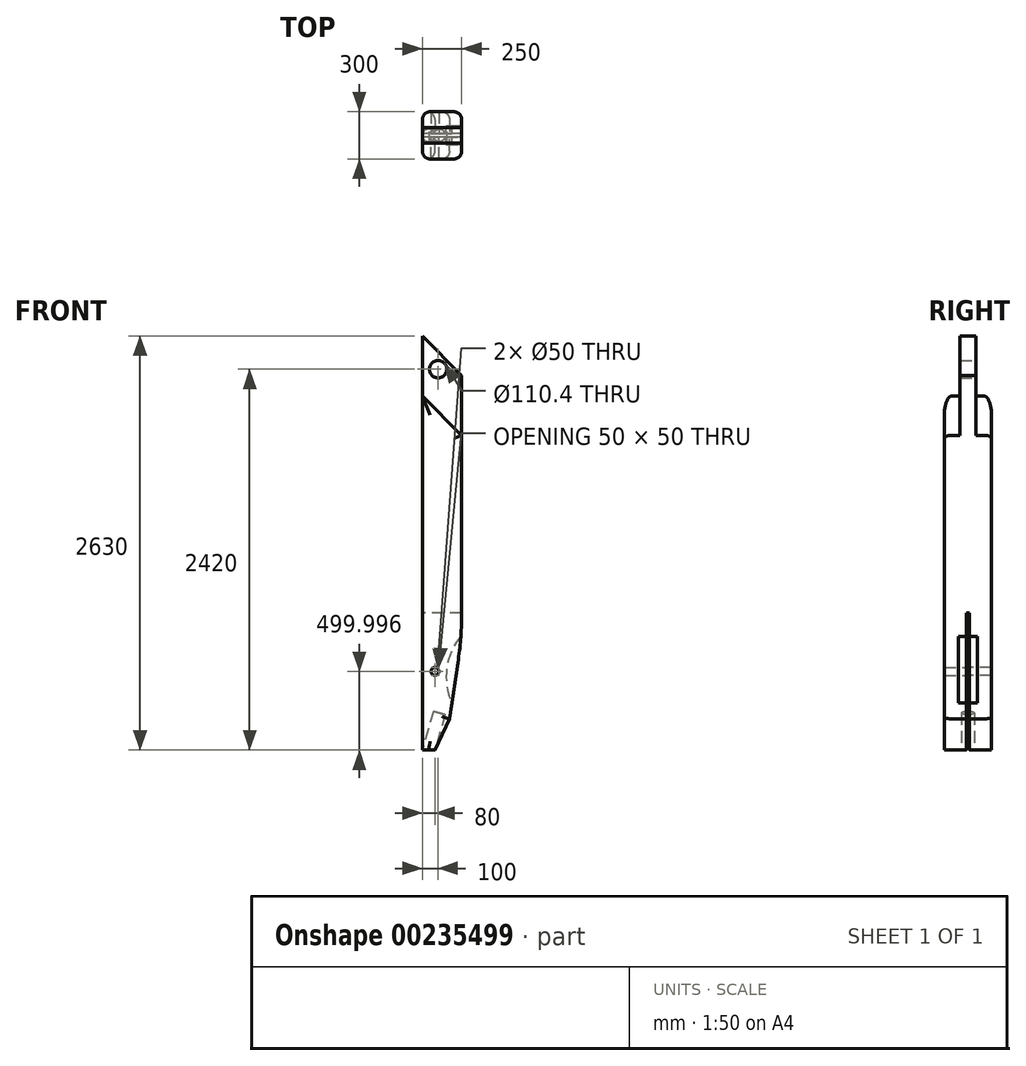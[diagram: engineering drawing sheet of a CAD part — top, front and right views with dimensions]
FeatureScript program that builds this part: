
annotation { "Feature Type Name" : "Feature", "Feature Type Description" : "" }
export const myFeature = defineFeature(function(context is Context, id is Id, definition is map)
    precondition{}
    {
        {
            var Q0;
            Q0=qCreatedBy(makeId("Front.planeOp"),FACE);
            var sketch = newSketch(context, id + "F0", { "sketchPlane" : qUnion([Q0])});
            skLineSegment(sketch, "E0", {"start": v(0, 1074.27) * mm, "end": v(0, -1175.73) * mm});
            skLineSegment(sketch, "E1", {"start": v(0, 1074.27) * mm, "end": v(0, 1454.27) * mm});
            skLineSegment(sketch, "E2", {"start": v(0, -1175.73) * mm, "end": v(80, -1175.73) * mm});
            skLineSegment(sketch, "E3", {"start": v(80, -1175.73) * mm, "end": v(172.42, -977.53) * mm});
            skLineSegment(sketch, "E4", {"start": v(250, -305.73) * mm, "end": v(250, 1204.27) * mm});
            skLineSegment(sketch, "E5", {"start": v(250, 1204.27) * mm, "end": v(0, 1454.27) * mm});
            skLineSegment(sketch, "E6", {"start": v(0, 1074.27) * mm, "end": v(250, 824.27) * mm});
            skCircle(sketch, "E7", {"center": v(80, -675.73) * mm, "radius": 25 * mm});
            skCircle(sketch, "E8", {"center": v(100, 1244.27) * mm, "radius": 55.2 * mm});
            skLineSegment(sketch, "E9", {"start": v(80, -532.98) * mm, "end": v(80, -1372.18) * mm, "construction": true});
            skLineSegment(sketch, "E10", {"start": v(0, 74.27) * mm, "end": v(250, 74.27) * mm, "construction": true});
            skLineSegment(sketch, "E11", {"start": v(172.42, -977.53) * mm, "end": v(228.5, -598.22) * mm});
            skArc(sketch, "E12", {"start": v(250, -305.73) * mm, "mid": v(244.62, -452.37) * mm, "end": v(228.5, -598.22) * mm});
            skSolve(sketch);
        }
        {
            var Q0;
            Q0=makeQuery(id+"F0.imprint","IMPRINT",FACE,{"disambiguationData":[TD([[makeQuery(id+"F0.imprint","IMPRINT",EDGE,{"derivedFrom":sQuery(id+"F0.wireOp",EDGE,"E0")}),1.0]])]});
            extrude(context, id + "F1", {"entities" : qUnion([Q0]), "depth" : 150 * mm});
        }
        {
            var Q0;
            Q0=makeQuery(id+"F0.imprint","IMPRINT",FACE,{"disambiguationData":[TD([[makeQuery(id+"F0.imprint","IMPRINT",EDGE,{"derivedFrom":sQuery(id+"F0.wireOp",EDGE,"E1")}),-1.0]])]});
            extrude(context, id + "F2", {"entities" : qUnion([Q0]), "operationType" : NewBodyOperationType.ADD, "depth" : 50 * mm});
        }
        {
            var Q0;
            Q0=makeQuery(id+"F2.boolean.opBoolean","MERGE",FACE,{"derivedFrom":[makeQuery(id+"F1.opExtrude","SWEPT_FACE",FACE,{"disambiguationData":[OSD([sQuery(id+"F0.wireOp",EDGE,"E0")])]}),makeQuery(id+"F2.opExtrude","SWEPT_FACE",FACE,{"disambiguationData":[OSD([sQuery(id+"F0.wireOp",EDGE,"E1")])]})]});
            var sketch = newSketch(context, id + "F3", { "sketchPlane" : qUnion([Q0])});
            skLineSegment(sketch, "E13.0", {"start": v(10, -305.73) * mm, "end": v(0, -305.73) * mm});
            skLineSegment(sketch, "E14", {"start": v(10, -305.73) * mm, "end": v(10, -1175.73) * mm});
            skPoint(sketch, "E15.orphan", {"position": v(150, -305.73) * mm});
            skLineSegment(sketch, "E16.0", {"start": v(0, -977.53) * mm, "end": v(0, -598.22) * mm});
            skLineSegment(sketch, "E17.0", {"start": v(0, -1175.73) * mm, "end": v(0, -977.53) * mm});
            skLineSegment(sketch, "E18.0", {"start": v(10, -1175.73) * mm, "end": v(0, -1175.73) * mm});
            skPoint(sketch, "E19.orphan", {"position": v(150, -1175.73) * mm});
            skLineSegment(sketch, "E20.0", {"start": v(0, -305.73) * mm, "end": v(0, -598.22) * mm});
            skSolve(sketch);
        }
        {
            var Q0;
            Q0 = qSketchRegion(id + "F3", true);
            extrude(context, id + "F4", {"entities" : qUnion([Q0]), "operationType" : NewBodyOperationType.REMOVE, "endBound" : BoundingType.THROUGH_ALL, "oppositeDirection" : true, "depth" : 25 * mm});
        }
        {
            var Q0;
            Q0=makeQuery(id+"F1.opExtrude","SWEPT_BODY",BODY,{"disambiguationData":[OSD([sQuery(id+"F0.wireOp",EDGE,"E0"),sQuery(id+"F0.wireOp",EDGE,"E2"),sQuery(id+"F0.wireOp",EDGE,"E3"),sQuery(id+"F0.wireOp",EDGE,"E4"),sQuery(id+"F0.wireOp",EDGE,"E6"),sQuery(id+"F0.wireOp",EDGE,"E7"),sQuery(id+"F0.wireOp",EDGE,"E11"),sQuery(id+"F0.wireOp",EDGE,"E12")])]});
            var Q1;
            Q1=qCreatedBy(makeId("Front.planeOp"),FACE);
            mirror(context, id + "F5", {"operationType" : NewBodyOperationType.ADD, "entities" : qUnion([Q0]), "mirrorPlane" : qUnion([Q1])});
        }
        {
            var Q0;
            Q0=makeQuery(id+"F5.opPattern","COPY",FACE,{"derivedFrom":makeQuery(id+"F1.opExtrude","CAP_FACE",FACE,{"disambiguationData":[OSD([sQuery(id+"F0.wireOp",EDGE,"E0"),sQuery(id+"F0.wireOp",EDGE,"E2"),sQuery(id+"F0.wireOp",EDGE,"E3"),sQuery(id+"F0.wireOp",EDGE,"E4"),sQuery(id+"F0.wireOp",EDGE,"E6"),sQuery(id+"F0.wireOp",EDGE,"E7"),sQuery(id+"F0.wireOp",EDGE,"E11"),sQuery(id+"F0.wireOp",EDGE,"E12")])],"isStart":false}),"instanceName":"1"});
            cPlane(context, id + "F6", {"entities" : qUnion([Q0]), "cplaneType" : CPlaneType.OFFSET, "offset" : 150 * mm, "oppositeDirection" : true, "width" : 150 * mm, "height" : 150 * mm});
        }
        {
            var Q0;
            Q0=qCreatedBy(id+"F6.planeOp",FACE);
            var sketch = newSketch(context, id + "F7", { "sketchPlane" : qUnion([Q0])});
            skLineSegment(sketch, "E21.0", {"start": v(-187.47, -875.73) * mm, "end": v(-228.5, -598.22) * mm});
            skPoint(sketch, "E22.0", {"position": v(-40, -1175.73) * mm});
            skPoint(sketch, "E23.0", {"position": v(-80, -1175.73) * mm});
            skPoint(sketch, "E24", {"position": v(-187.47, -875.73) * mm});
            skPoint(sketch, "E25.0", {"position": v(0, -1175.73) * mm});
            skPoint(sketch, "E26.0.start.orphan", {"position": v(-250, -305.73) * mm});
            skPoint(sketch, "E27.orphan", {"position": v(-172.42, -977.53) * mm});
            skPoint(sketch, "E28.0", {"position": v(-244.62, -452.37) * mm});
            skArc(sketch, "E29", {"start": v(-187.47, -875.73) * mm, "mid": v(-154.8, -655.78) * mm, "end": v(-244.62, -452.37) * mm});
            skLineSegment(sketch, "E30", {"start": v(-228.5, -598.22) * mm, "end": v(-244.62, -452.37) * mm});
            skLineSegment(sketch, "E31", {"start": v(0, -1175.73) * mm, "end": v(-154.8, -640.2) * mm, "construction": true});
            skPoint(sketch, "E31.endSnap0", {"position": v(-154.8, -655.78) * mm});
            skLineSegment(sketch, "E32", {"start": v(0, -1175.73) * mm, "end": v(-357.55, -1279.08) * mm, "construction": true});
            skLineSegment(sketch, "E33", {"start": v(-244.62, -452.37) * mm, "end": v(-337.43, -462.63) * mm});
            skLineSegment(sketch, "E34", {"start": v(-337.43, -462.63) * mm, "end": v(-289.76, -893.9) * mm});
            skLineSegment(sketch, "E35", {"start": v(-289.76, -893.9) * mm, "end": v(-187.47, -875.73) * mm});
            skSolve(sketch);
        }
        {
            var Q0;
            Q0=makeQuery(id+"F7.imprint","IMPRINT",FACE,{"disambiguationData":[TD([[makeQuery(id+"F7.imprint","IMPRINT",EDGE,{"derivedFrom":sQuery(id+"F7.wireOp",EDGE,"E21.0")}),-1.0]])]});
            var Q1;
            Q1=makeQuery(id+"F7.imprint","IMPRINT",FACE,{"disambiguationData":[TD([[makeQuery(id+"F7.imprint","IMPRINT",EDGE,{"derivedFrom":sQuery(id+"F7.wireOp",EDGE,"E21.0")}),1.0]])]});
            extrude(context, id + "F8", {"entities" : qUnion([Q0, Q1]), "operationType" : NewBodyOperationType.REMOVE, "endBound" : BoundingType.SYMMETRIC, "oppositeDirection" : true, "depth" : 120 * mm});
        }
        {
            var Q0;
            Q0=sQuery(id+"F7.wireOp",EDGE,"E32");
            var Q1;
            Q1=sQuery(id+"F7.wireOp",EDGE,"E31");
            cPlane(context, id + "F9", {"entities" : qUnion([Q0, Q1]), "cplaneType" : CPlaneType.LINE_ANGLE, "offset" : 25 * mm, "angle" : 90 * degree, "width" : 150 * mm, "height" : 150 * mm});
        }
        {
            var Q0;
            Q0=qCreatedBy(id+"F9.planeOp",FACE);
            var sketch = newSketch(context, id + "F10", { "sketchPlane" : qUnion([Q0])});
            skCircle(sketch, "E36", {"center": v(364.9, 0) * mm, "radius": 40 * mm});
            skSolve(sketch);
        }
        {
            var Q0;
            Q0=makeQuery(id+"F10.imprint","IMPRINT",FACE,{"disambiguationData":[TD([[makeQuery(id+"F10.imprint","IMPRINT",EDGE,{"derivedFrom":sQuery(id+"F10.wireOp",EDGE,"E36")}),1.0]])]});
            extrude(context, id + "F11", {"entities" : qUnion([Q0]), "operationType" : NewBodyOperationType.REMOVE, "oppositeDirection" : true, "depth" : 257 * mm});
        }
        {
            var Q0;
            Q0=makeQuery(id+"F1.opExtrude","CAP_EDGE",EDGE,{"disambiguationData":[OSD([sQuery(id+"F0.wireOp",EDGE,"E4")])],"isStart":false});
            var Q1;
            Q1=makeQuery(id+"F1.opExtrude","CAP_EDGE",EDGE,{"disambiguationData":[OSD([sQuery(id+"F0.wireOp",EDGE,"E0")])],"isStart":false});
            var Q2;
            Q2=makeQuery(id+"F1.opExtrude","CAP_EDGE",EDGE,{"disambiguationData":[OSD([sQuery(id+"F0.wireOp",EDGE,"E6")])],"isStart":false});
            var Q3;
            Q3=makeQuery(id+"F1.opExtrude","CAP_EDGE",EDGE,{"disambiguationData":[OSD([sQuery(id+"F0.wireOp",EDGE,"E3")])],"isStart":false});
            var Q4;
            Q4=makeQuery(id+"F1.opExtrude","CAP_EDGE",EDGE,{"disambiguationData":[OSD([sQuery(id+"F0.wireOp",EDGE,"E2")])],"isStart":false});
            var Q5;
            Q5=makeQuery(id+"F5.opPattern","COPY",EDGE,{"derivedFrom":makeQuery(id+"F1.opExtrude","CAP_EDGE",EDGE,{"disambiguationData":[OSD([sQuery(id+"F0.wireOp",EDGE,"E6")])],"isStart":false}),"instanceName":"1"});
            var Q6;
            Q6=makeQuery(id+"F5.opPattern","COPY",EDGE,{"derivedFrom":makeQuery(id+"F1.opExtrude","CAP_EDGE",EDGE,{"disambiguationData":[OSD([sQuery(id+"F0.wireOp",EDGE,"E4")])],"isStart":false}),"instanceName":"1"});
            var Q7;
            Q7=makeQuery(id+"F5.opPattern","COPY",EDGE,{"derivedFrom":makeQuery(id+"F1.opExtrude","CAP_EDGE",EDGE,{"disambiguationData":[OSD([sQuery(id+"F0.wireOp",EDGE,"E0")])],"isStart":false}),"instanceName":"1"});
            var Q8;
            Q8=makeQuery(id+"F5.opPattern","COPY",EDGE,{"derivedFrom":makeQuery(id+"F1.opExtrude","CAP_EDGE",EDGE,{"disambiguationData":[OSD([sQuery(id+"F0.wireOp",EDGE,"E2")])],"isStart":false}),"instanceName":"1"});
            var Q9;
            Q9=makeQuery(id+"F5.opPattern","COPY",EDGE,{"derivedFrom":makeQuery(id+"F1.opExtrude","CAP_EDGE",EDGE,{"disambiguationData":[OSD([sQuery(id+"F0.wireOp",EDGE,"E3")])],"isStart":false}),"instanceName":"1"});
            fillet(context, id + "F12", {"entities" : qUnion([Q0, Q1, Q2, Q3, Q4, Q5, Q6, Q7, Q8, Q9]), "radius" : 50 * mm, "tangentPropagation" : true, "allowEdgeOverflow" : false});
        }
    });
